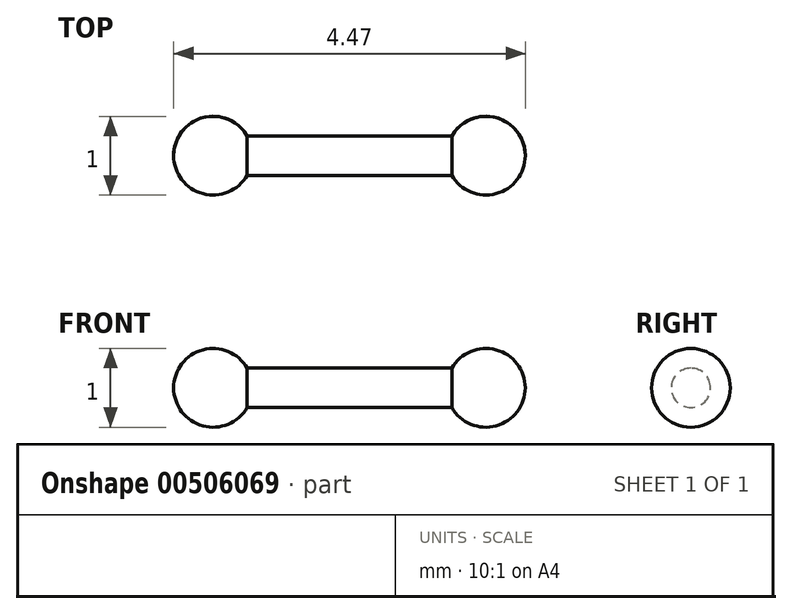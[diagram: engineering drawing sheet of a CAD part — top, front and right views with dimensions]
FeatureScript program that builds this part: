
annotation { "Feature Type Name" : "Feature", "Feature Type Description" : "" }
export const myFeature = defineFeature(function(context is Context, id is Id, definition is map)
    precondition{}
    {
        {
            var Q0;
            Q0=qCreatedBy(makeId("Top.planeOp"),FACE);
            var sketch = newSketch(context, id + "F0", { "sketchPlane" : qUnion([Q0])});
            skArc(sketch, "E0", {"start": v(0.43, 0.25) * mm, "mid": v(-0.13, 0.48) * mm, "end": v(-0.5, 0) * mm});
            skLineSegment(sketch, "E1", {"start": v(0.43, 0.25) * mm, "end": v(1.73, 0.25) * mm});
            skLineSegment(sketch, "E2", {"start": v(0, 0) * mm, "end": v(0.5, 0) * mm});
            skLineSegment(sketch, "E3", {"start": v(1.73, 0.25) * mm, "end": v(1.73, 0) * mm});
            skLineSegment(sketch, "E4", {"start": v(1.73, 0) * mm, "end": v(0.5, 0) * mm});
            skLineSegment(sketch, "E5", {"start": v(0, 0) * mm, "end": v(-0.5, 0) * mm});
            skSolve(sketch);
        }
        {
            var Q0;
            Q0 = qSketchRegion(id + "F0", true);
            var Q1;
            Q1=sQuery(id+"F0.wireOp",EDGE,"E2");
            revolve(context, id + "F1", {"entities" : qUnion([Q0]), "axis" : qUnion([Q1]), "revolveType" : RevolveType.FULL});
        }
        {
            var Q0;
            Q0=makeQuery(id+"F1.opRevolve","SWEPT_BODY",BODY,{"disambiguationData":[OSD([sQuery(id+"F0.wireOp",EDGE,"E0"),sQuery(id+"F0.wireOp",EDGE,"E1"),sQuery(id+"F0.wireOp",EDGE,"E2"),sQuery(id+"F0.wireOp",EDGE,"E3"),sQuery(id+"F0.wireOp",EDGE,"E4"),sQuery(id+"F0.wireOp",EDGE,"E5")])]});
            var Q1;
            Q1=makeQuery(id+"F1.opRevolve","SWEPT_FACE",FACE,{"disambiguationData":[OSD([sQuery(id+"F0.wireOp",EDGE,"E3")])]});
            mirror(context, id + "F2", {"operationType" : NewBodyOperationType.ADD, "entities" : qUnion([Q0]), "mirrorPlane" : qUnion([Q1])});
        }
    });
